# Revit family: Lighting_Fixture-Wall-Astro-Venetoxxxx
name_source: partatom
category: Lighting Fixtures
revit_build: Autodesk Revit LT 2014 (Build: 20130308_1515(x64)
units: mm (PartAtom-declared; Revit-internal decimal feet)

## types (2) — shared parameters
Assembly Code = D5020200
Casing Material = Astro - Plaster - White
Class = 1
Color Filter = 16777215
Description = Wall Light
Dimmable = No
Dimming Lamp Color Temperature Shift = <None>
Emit from Line Length = 250 mm  [stored 0.82021 ft]
Height = 65 mm  [stored 0.213255 ft]
IP Rating = IP20
Lamp = 2G11
Lamp included = No
Length = 105 mm  [stored 0.344488 ft]
Light Source Elevation = 1590 mm  [stored 5.21654 ft]
Light Source From Wall = 350 mm  [stored 1.14829 ft]
Luminaire Lamp Efficiency Rating = -B
Manufacturer = Astro Lighting Ltd, CM20 2DP
Mountable on normally flammable surfaces = Yes
Number of Poles = 1
Product Documentation = http://www.astrolighting.co.uk
Suitable for bathroom zone = Zone 3
Tilt Angle = -90.00°
URL = www.astrolighting.co.uk
Voltage = 230 V

## per-type parameters (varying)
| type | Apparent Load | Backplate Width | Cable Placement Left | Cable Placement Top | Cutout Width | Model | Photometric Web File | Type Comments | Wattage Comments | Weight | Width |
| 0609 Veneto 300 | 13 VA | 200 mm  [stored 0.656168 ft] | 39 mm  [stored 0.127953 ft] | 13.5 mm  [stored 0.0442913 ft] | 220 mm  [stored 0.721785 ft] | 0609 Veneto 300 | 0609 VENETO 300.ies | Includes internal electronic ballast. | 18w | 1.5kg | 300 mm |
| 0610 Veneto 400 | 24 VA | 300 mm | 99 mm  [stored 0.324803 ft] | 35 mm  [stored 0.114829 ft] | 320 mm  [stored 1.04987 ft] | 0609 Veneto 400 | 0610 VENETO 400.ies | Includes internal electronic ballast. Unsuitable for frequent switching. | 24w | 1.8kg | 400 mm  [stored 1.31234 ft] |

note: [stored X ft] marks values corroborated as IEEE doubles in the binary element streams (Revit-internal decimal feet)

## geometry (parser evidence)
native form markers: Sweep x1
no freeform markers — native parametric forms only
